# Revit family: 75210XXX_new
name_source: partatom
category: Plumbing Fixtures
revit_build: Autodesk Revit 2018 (Build: 20170223_1515(x64)
units: mm (PartAtom-declared; Revit-internal decimal feet)

## family parameters
Always vertical = No
Cut with Voids When Loaded = No
Part Type = Normal
Room Calculation Point = No
Round Connector Dimension = Use Diameter
Shared = No
Work Plane-Based = Yes

## types (1)
- 000 Chrome
    Always visible = Yes
    BIMobject category = Wash Basins
    Default Elevation = 1219.2 mm  [stored 4 ft]
    Design country = Germany
    EAN code = 4059625395240
    Edition number = 1
    GTIN code = https://4059625395240
    IFC Classification = Sanitary Terminal
    Installation instructions = https://www.hansgrohe.com
    Manufacturer country = Germany
    Manufacturer name = hansgrohe
    Material 1 = Hansgrohe - Vivenis - 000 Chrome
    Material 2 = Hansgrohe - Vivenis - Gray
    NBS Reference Code = 31-75
    NBS Reference Description = Sanitary Accessories
    Product Guid = 669565bd-be40-4e7e-94d1-e5e782357c42
    Product SKU = 75210XXX
    Product data url = https://www.bimobject.com
    Product family = Vivenis
    Product group = Basin mixers
    Product name = 75210XXX Vivenis Single lever basin mixer with bidette hand shower and shower hose 160 cm
    Product url = https://www.hansgrohe.com
    QR code = https://www.bimobject.com
    Technical description = https://www.hansgrohe.com
    UNSPSC Code = 301815
    Weight Net (Kg) = 2,2

note: [stored X ft] marks values corroborated as IEEE doubles in the binary element streams (Revit-internal decimal feet)

## geometry (parser evidence)
native form markers: Sweep x2
no freeform markers — native parametric forms only
